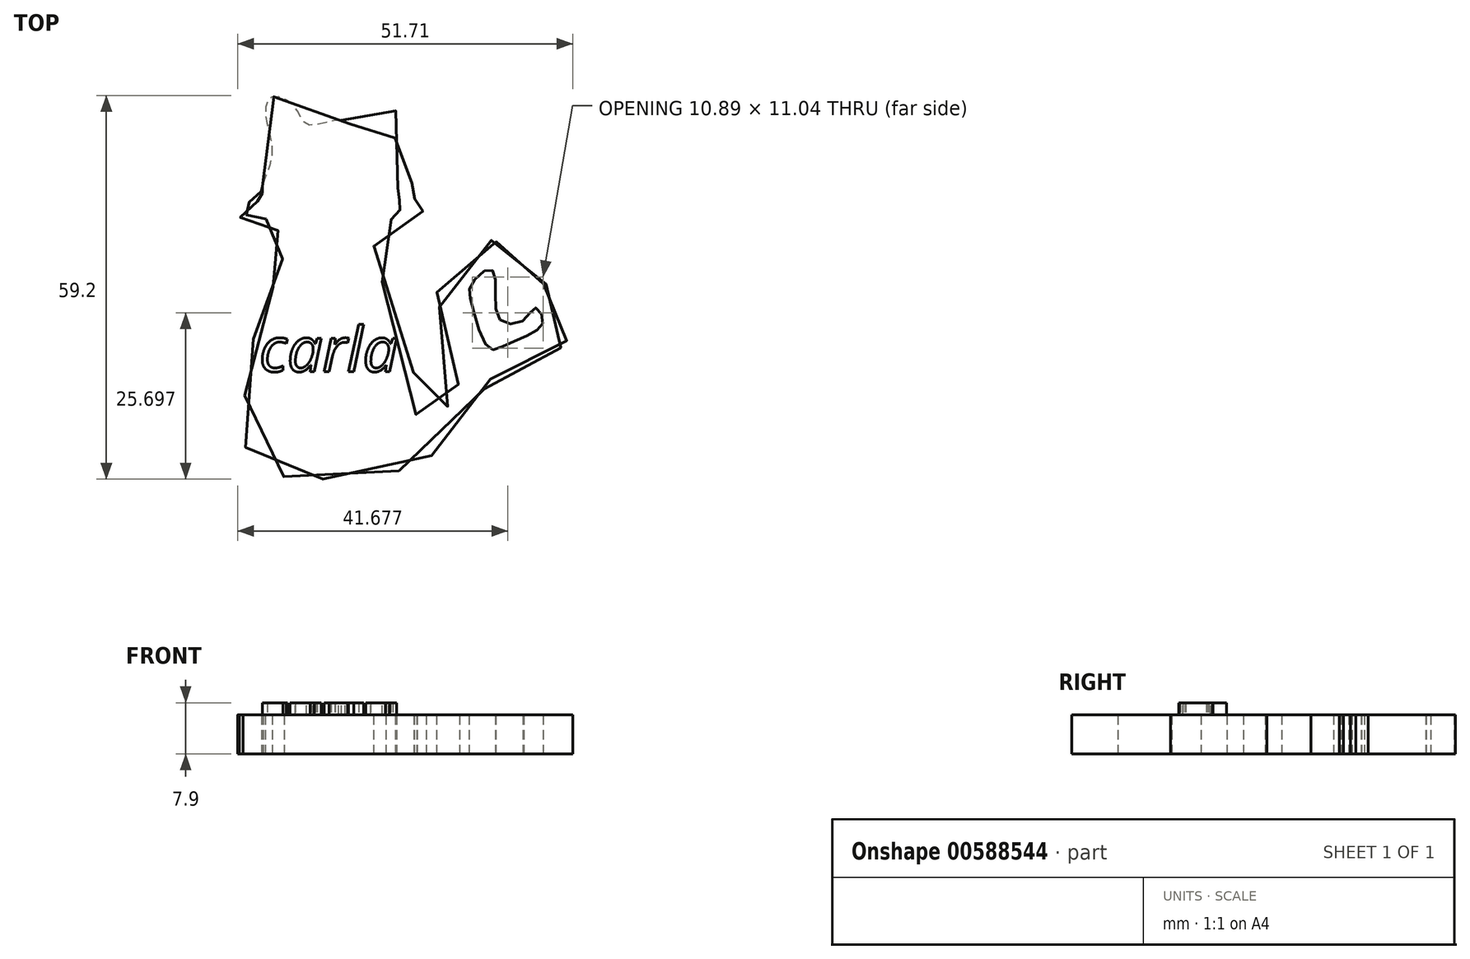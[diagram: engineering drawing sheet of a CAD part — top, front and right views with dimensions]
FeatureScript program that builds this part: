
annotation { "Feature Type Name" : "Feature", "Feature Type Description" : "" }
export const myFeature = defineFeature(function(context is Context, id is Id, definition is map)
    precondition{}
    {
        {
            var Q0;
            Q0=qCreatedBy(makeId("Top.planeOp"),FACE);
            var sketch = newSketch(context, id + "F0", { "sketchPlane" : qUnion([Q0])});
            skFitSpline(sketch, "E0", {"points": [v(-47.7, 45.04) * mm, v(-47.7, 44.64) * mm, v(-49.08, 44.7) * mm, v(-51.11, 45.04) * mm, v(-51.36, 44.86) * mm, v(-49.36, 44.37) * mm, v(-47.73, 44.21) * mm, v(-47.82, 43.72) * mm, v(-47.82, 43.32) * mm, v(-49.14, 43.07) * mm, v(-51.27, 43.1) * mm, v(-51.51, 42.8) * mm, v(-49.76, 42.67) * mm, v(-48.43, 42.8) * mm, v(-47.73, 42.98) * mm, v(-47.76, 42.27) * mm, v(-47.57, 41.65) * mm, v(-48.46, 41.32) * mm, v(-49.67, 40.76) * mm, v(-50.8, 40.58) * mm, v(-51.27, 40.33) * mm, v(-50.44, 40.42) * mm, v(-48.46, 41.1) * mm, v(-47.54, 41.4) * mm, v(-47.39, 40.8) * mm, v(-46.99, 39.84) * mm, v(-45.9, 38.64) * mm, v(-44.98, 38.02) * mm, v(-44.52, 37.13) * mm, v(-44.34, 36.23) * mm, v(-44.46, 34.57) * mm, v(-45.23, 31.61) * mm, v(-46.22, 29.2) * mm, v(-48.56, 23.6) * mm, v(-49.95, 16.64) * mm, v(-50.65, 9.32) * mm, v(-49.6, 2.96) * mm, v(-46.47, 0.78) * mm, v(-41.59, 0) * mm, v(-33.83, 0) * mm, v(-27.12, 1.04) * mm, v(-19.2, 5.05) * mm, v(-14.83, 9.84) * mm, v(-12.74, 15.33) * mm, v(-11.96, 15.16) * mm, v(-6.9, 17.07) * mm, v(-1.94, 19.95) * mm, v(0, 22.91) * mm, v(0, 26.22) * mm, v(-1.07, 28.49) * mm, v(-4.55, 30.06) * mm, v(-7.34, 29.88) * mm, v(-7.43, 32.24) * mm, v(-9.95, 35.72) * mm, v(-14.22, 36.77) * mm, v(-18.58, 34.07) * mm, v(-20.76, 30.15) * mm, v(-19.71, 24.48) * mm, v(-17.88, 20.56) * mm, v(-17.62, 13.94) * mm, v(-21.46, 8.7) * mm, v(-24.16, 7.05) * mm, v(-23.98, 10.02) * mm, v(-25.73, 21.7) * mm, v(-29.74, 31.71) * mm, v(-30.52, 35.98) * mm, v(-30, 38.08) * mm, v(-29.13, 38.25) * mm, v(-27.03, 41.04) * mm, v(-24.6, 41.35) * mm, v(-22.42, 41.35) * mm, v(-23.87, 41.87) * mm, v(-27.08, 41.56) * mm, v(-26.77, 42.8) * mm, v(-25.42, 42.9) * mm, v(-23.87, 43.42) * mm, v(-24.18, 43.73) * mm, v(-26.77, 43) * mm, v(-26.87, 44.25) * mm, v(-25.21, 44.77) * mm, v(-24.28, 45.5) * mm, v(-25.32, 45.5) * mm, v(-26.66, 44.67) * mm, v(-27.29, 46.63) * mm, v(-28.64, 49.56) * mm, v(-27.24, 52.7) * mm, v(-28.29, 58.97) * mm, v(-31.77, 57.05) * mm, v(-33.69, 54.61) * mm, v(-35.6, 55.3) * mm, v(-40.66, 54.61) * mm, v(-42.75, 57.4) * mm, v(-46.41, 58.8) * mm, v(-47.1, 55.3) * mm, v(-46.24, 49.9) * mm, v(-47.7, 45.04) * mm]});
            skFitSpline(sketch, "E1", {"points": [v(-11.03, 24.48) * mm, v(-11.73, 29.88) * mm, v(-12.6, 32.3) * mm, v(-15.56, 29.88) * mm, v(-15.39, 26.9) * mm, v(-12.77, 20.1) * mm, v(-10.16, 20.63) * mm, v(-5.63, 22.72) * mm, v(-4.4, 24.48) * mm, v(-5.63, 26.38) * mm, v(-7.34, 24.48) * mm, v(-11.03, 24.48) * mm]});
            skSolve(sketch);
        }
        {
            var Q0;
            Q0=makeQuery(id+"F0.imprint","IMPRINT",FACE,{"disambiguationData":[TD([[makeQuery(id+"F0.imprint","IMPRINT",EDGE,{"derivedFrom":sQuery(id+"F0.wireOp",EDGE,"E0")}),1.0]])]});
            extrude(context, id + "F1", {"entities" : qUnion([Q0]), "depth" : 6 * mm, "offsetDistance" : 25 * mm});
        }
        {
            var Q0;
            Q0=qCreatedBy(makeId("Top.planeOp"),FACE);
            var sketch = newSketch(context, id + "F2", { "sketchPlane" : qUnion([Q0])});
            skText(sketch, "E2", { "text": "carla", "fontName": "OpenSans-Italic.ttf"});
            const initialGuessF2  = {"E2": [-0.04819, 0.01651, 1, 0, 0.0069]};
            skSetInitialGuess(sketch, initialGuessF2);
            skSolve(sketch);
        }
        {
            var Q0;
            Q0 = qSketchRegion(id + "F2", true);
            extrude(context, id + "F3", {"entities" : qUnion([Q0]), "operationType" : NewBodyOperationType.ADD, "depth" : 7.9 * mm, "offsetDistance" : 25 * mm});
        }
    });
